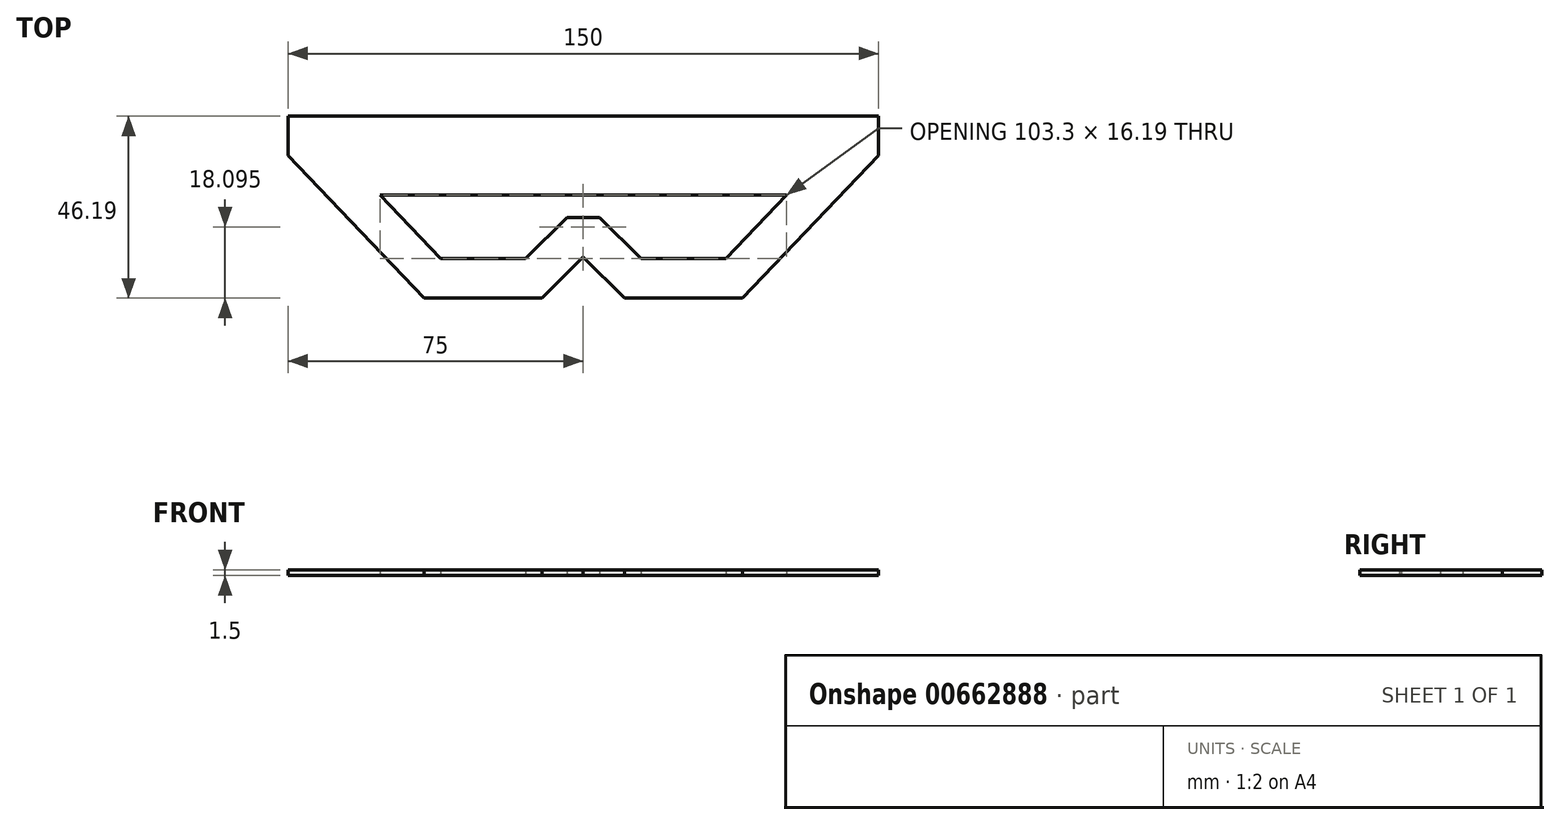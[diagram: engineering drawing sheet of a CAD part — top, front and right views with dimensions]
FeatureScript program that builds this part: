
annotation { "Feature Type Name" : "Feature", "Feature Type Description" : "" }
export const myFeature = defineFeature(function(context is Context, id is Id, definition is map)
    precondition{}
    {
        {
            var Q0;
            Q0=qCreatedBy(makeId("Top.planeOp"),FACE);
            var sketch = newSketch(context, id + "F0", { "sketchPlane" : qUnion([Q0])});
            skLineSegment(sketch, "E0", {"start": v(-75, 0) * mm, "end": v(75, 0) * mm});
            skLineSegment(sketch, "E1", {"start": v(75, 0) * mm, "end": v(75, -10) * mm});
            skLineSegment(sketch, "E2", {"start": v(75, -10) * mm, "end": v(40.5, -46.2) * mm});
            skLineSegment(sketch, "E3", {"start": v(40.5, -46.2) * mm, "end": v(10.5, -46.2) * mm});
            skLineSegment(sketch, "E4", {"start": v(10.5, -46.2) * mm, "end": v(0, -35.7) * mm});
            skLineSegment(sketch, "E5", {"start": v(0, -35.7) * mm, "end": v(-10.5, -46.2) * mm});
            skLineSegment(sketch, "E6", {"start": v(-10.5, -46.2) * mm, "end": v(-40.5, -46.2) * mm});
            skLineSegment(sketch, "E7", {"start": v(-40.5, -46.2) * mm, "end": v(-75, -10) * mm});
            skLineSegment(sketch, "E8", {"start": v(-75, -10) * mm, "end": v(-75, 0) * mm});
            skLineSegment(sketch, "E9.1", {"start": v(-36.22, -36.2) * mm, "end": v(-51.65, -20) * mm});
            skLineSegment(sketch, "E9.2", {"start": v(-14.64, -36.2) * mm, "end": v(-36.22, -36.2) * mm});
            skLineSegment(sketch, "E9.3", {"start": v(-4.14, -25.7) * mm, "end": v(-14.64, -36.2) * mm});
            skLineSegment(sketch, "E9.5", {"start": v(51.65, -20) * mm, "end": v(36.22, -36.2) * mm});
            skLineSegment(sketch, "E9.6", {"start": v(36.22, -36.2) * mm, "end": v(14.64, -36.2) * mm});
            skLineSegment(sketch, "E9.7", {"start": v(14.64, -36.2) * mm, "end": v(4.14, -25.7) * mm});
            skLineSegment(sketch, "E10.trimOffspring", {"start": v(-51.65, -20) * mm, "end": v(51.65, -20) * mm});
            skLineSegment(sketch, "E11", {"start": v(-4.14, -25.7) * mm, "end": v(4.14, -25.7) * mm});
            skSolve(sketch);
        }
        {
            var Q0;
            Q0 = qSketchRegion(id + "F0", true);
            extrude(context, id + "F1", {"entities" : qUnion([Q0]), "depth" : 1.5 * mm, "offsetDistance" : 25 * mm});
        }
    });
